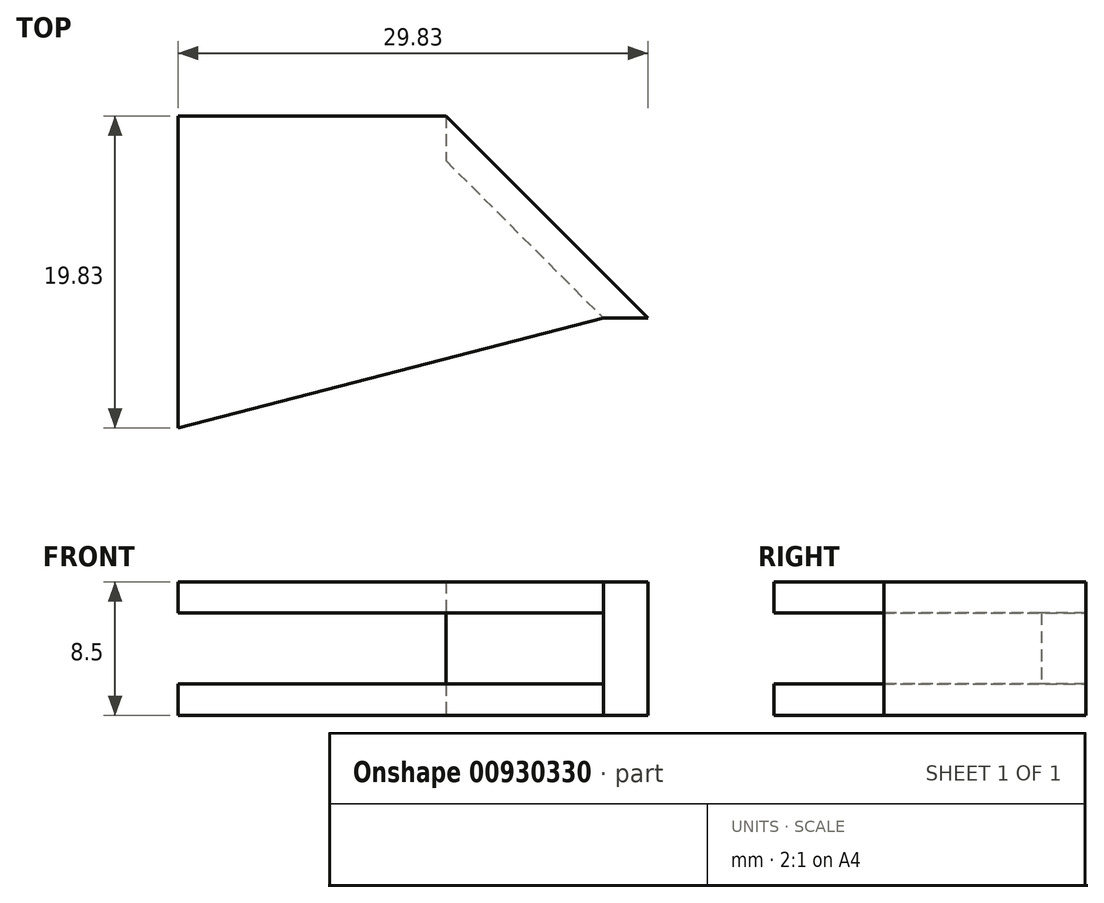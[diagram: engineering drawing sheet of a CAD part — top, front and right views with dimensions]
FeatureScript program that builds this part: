
annotation { "Feature Type Name" : "Feature", "Feature Type Description" : "" }
export const myFeature = defineFeature(function(context is Context, id is Id, definition is map)
    precondition{}
    {
        {
            var Q0;
            Q0=qCreatedBy(makeId("Top.planeOp"),FACE);
            var sketch = newSketch(context, id + "F0", { "sketchPlane" : qUnion([Q0])});
            skLineSegment(sketch, "E0", {"start": v(0, 0) * mm, "end": v(-27, 0) * mm});
            skLineSegment(sketch, "E1", {"start": v(-27, 0) * mm, "end": v(-27, 10) * mm});
            skLineSegment(sketch, "E2", {"start": v(-10, 10) * mm, "end": v(0, 0) * mm});
            skLineSegment(sketch, "E3", {"start": v(0, 0) * mm, "end": v(-27, -7) * mm});
            skLineSegment(sketch, "E4", {"start": v(-27, -7) * mm, "end": v(-27, 0) * mm});
            skLineSegment(sketch, "E5", {"start": v(-27, 10) * mm, "end": v(-10, 10) * mm});
            skLineSegment(sketch, "E6", {"start": v(-10, 12.83) * mm, "end": v(2.83, 0) * mm});
            skLineSegment(sketch, "E7", {"start": v(2.83, 0) * mm, "end": v(0, 0) * mm});
            skLineSegment(sketch, "E8", {"start": v(-10, 10) * mm, "end": v(-10, 12.83) * mm});
            skLineSegment(sketch, "E9", {"start": v(-10, 12.83) * mm, "end": v(-27, 12.83) * mm});
            skLineSegment(sketch, "E10", {"start": v(-27, 12.83) * mm, "end": v(-27, 10) * mm});
            skSolve(sketch);
        }
        {
            var Q0;
            Q0=makeQuery(id+"F0.imprint","IMPRINT",FACE,{"disambiguationData":[TD([[makeQuery(id+"F0.imprint","IMPRINT",EDGE,{"derivedFrom":sQuery(id+"F0.wireOp",EDGE,"E0")}),-1.0]])]});
            var Q1;
            Q1 = qSketchRegion(id + "F0", true);
            extrude(context, id + "F1", {"entities" : qUnion([Q0, Q1]), "depth" : 8.5 * mm, "offsetDistance" : 25 * mm});
        }
        {
            var Q0;
            Q0=qCreatedBy(makeId("Top.planeOp"),FACE);
            var sketch = newSketch(context, id + "F2", { "sketchPlane" : qUnion([Q0])});
            skLineSegment(sketch, "E11", {"start": v(0, 0) * mm, "end": v(-27, 0) * mm});
            skLineSegment(sketch, "E12", {"start": v(-27, 0) * mm, "end": v(-27, 10) * mm});
            skLineSegment(sketch, "E13", {"start": v(-10, 10) * mm, "end": v(0, 0) * mm});
            skLineSegment(sketch, "E14", {"start": v(0, 0) * mm, "end": v(-27, -7) * mm});
            skLineSegment(sketch, "E15", {"start": v(-27, -7) * mm, "end": v(-27, 0) * mm});
            skLineSegment(sketch, "E16", {"start": v(-27, 10) * mm, "end": v(-10, 10) * mm});
            skLineSegment(sketch, "E17", {"start": v(-27, 10) * mm, "end": v(-27, 13.28) * mm});
            skLineSegment(sketch, "E18", {"start": v(-27, 13.28) * mm, "end": v(-10, 13.28) * mm});
            skLineSegment(sketch, "E19", {"start": v(-10, 13.28) * mm, "end": v(-10, 10) * mm});
            skSolve(sketch);
        }
        {
            var Q0;
            Q0 = qSketchRegion(id + "F2", true);
            extrude(context, id + "F3", {"entities" : qUnion([Q0]), "operationType" : NewBodyOperationType.REMOVE, "depth" : 6.5 * mm, "offsetDistance" : 25 * mm, "hasSecondDirection" : true, "secondDirectionOppositeDirection" : true, "secondDirectionDepth" : -2 * mm});
        }
    });
